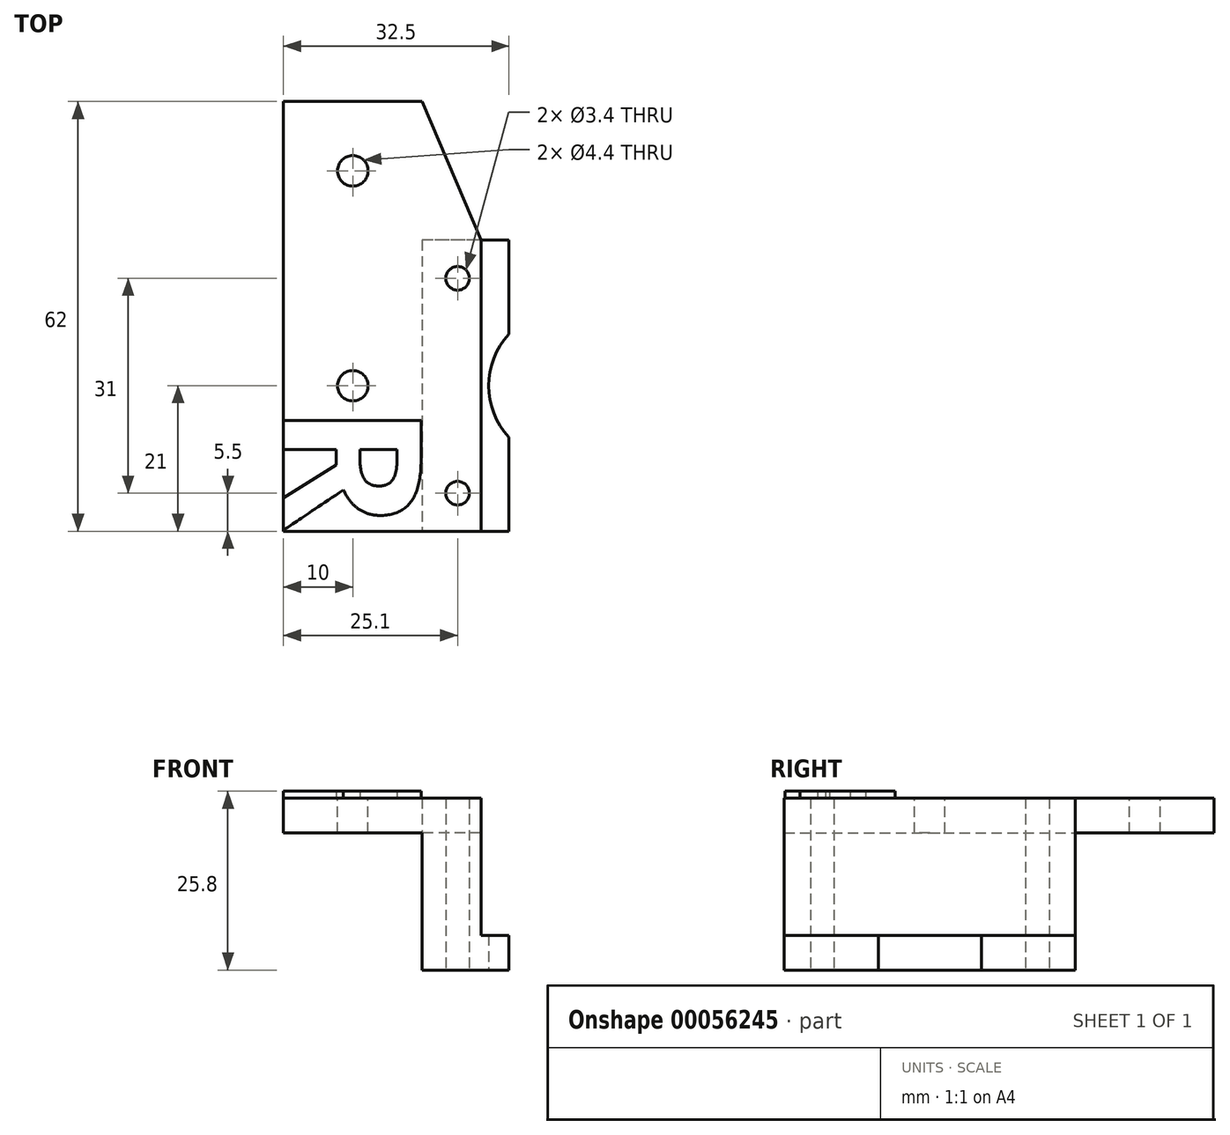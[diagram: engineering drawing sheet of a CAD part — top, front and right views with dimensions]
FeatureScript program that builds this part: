
annotation { "Feature Type Name" : "Feature", "Feature Type Description" : "" }
export const myFeature = defineFeature(function(context is Context, id is Id, definition is map)
    precondition{}
    {
        {
            var Q0;
            Q0=qCreatedBy(makeId("Front.planeOp"),FACE);
            var sketch = newSketch(context, id + "F0", { "sketchPlane" : qUnion([Q0])});
            skLineSegment(sketch, "E0", {"start": v(8.5, 24.8) * mm, "end": v(8.5, 5) * mm});
            skLineSegment(sketch, "E1", {"start": v(8.5, 5) * mm, "end": v(12.5, 5) * mm});
            skLineSegment(sketch, "E2", {"start": v(12.5, 5) * mm, "end": v(12.5, 0) * mm});
            skLineSegment(sketch, "E3", {"start": v(12.5, 0) * mm, "end": v(0, 0) * mm});
            skLineSegment(sketch, "E4", {"start": v(0, 0) * mm, "end": v(0, 24.8) * mm});
            skLineSegment(sketch, "E5", {"start": v(0, 24.8) * mm, "end": v(8.5, 24.8) * mm});
            skSolve(sketch);
        }
        {
            var Q0;
            Q0=qSketchRegion(id+"F0",true);
            extrude(context, id + "F1", {"entities" : qUnion([Q0]), "oppositeDirection" : true, "depth" : 42 * mm});
        }
        {
            var Q0;
            Q0=makeQuery(id+"F1.opExtrude","SWEPT_FACE",FACE,{"disambiguationData":[OSD([sQuery(id+"F0.wireOp",EDGE,"E3")])]});
            var sketch = newSketch(context, id + "F2", { "sketchPlane" : qUnion([Q0])});
            skCircle(sketch, "E6", {"center": v(5.1, -5.5) * mm, "radius": 1.7 * mm});
            skCircle(sketch, "E7", {"center": v(5.1, -36.5) * mm, "radius": 1.7 * mm});
            skCircle(sketch, "E8", {"center": v(20.6, -21) * mm, "radius": 11 * mm});
            skLineSegment(sketch, "E9", {"start": v(0, -21) * mm, "end": v(12.5, -21) * mm, "construction": true});
            skSolve(sketch);
        }
        {
            var Q0;
            Q0=qSketchRegion(id+"F2",true);
            extrude(context, id + "F3", {"entities" : qUnion([Q0]), "operationType" : NewBodyOperationType.REMOVE, "endBound" : BoundingType.THROUGH_ALL, "oppositeDirection" : true, "depth" : 25 * mm});
        }
        {
            var Q0;
            Q0=makeQuery(id+"F1.opExtrude","SWEPT_FACE",FACE,{"disambiguationData":[OSD([sQuery(id+"F0.wireOp",EDGE,"E4")])]});
            var sketch = newSketch(context, id + "F4", { "sketchPlane" : qUnion([Q0])});
            skLineSegment(sketch, "E10.bottom", {"start": v(0, 24.8) * mm, "end": v(-62, 24.8) * mm});
            skLineSegment(sketch, "E10.top", {"start": v(0, 19.8) * mm, "end": v(-62, 19.8) * mm});
            skLineSegment(sketch, "E10.left", {"start": v(0, 24.8) * mm, "end": v(0, 19.8) * mm});
            skLineSegment(sketch, "E10.right", {"start": v(-62, 24.8) * mm, "end": v(-62, 19.8) * mm});
            skSolve(sketch);
        }
        {
            var Q0;
            Q0=qSketchRegion(id+"F4",true);
            extrude(context, id + "F5", {"entities" : qUnion([Q0]), "operationType" : NewBodyOperationType.ADD, "depth" : 20 * mm});
        }
        {
            var Q0;
            Q0=makeQuery(id+"F5.boolean.opBoolean","MERGE",FACE,{"derivedFrom":[makeQuery(id+"F1.opExtrude","SWEPT_FACE",FACE,{"disambiguationData":[OSD([sQuery(id+"F0.wireOp",EDGE,"E5")])]}),makeQuery(id+"F5.opExtrude","SWEPT_FACE",FACE,{"disambiguationData":[OSD([sQuery(id+"F4.wireOp",EDGE,"0187bcc0-72c3-49ed-8d9d-e556f2aca4c1.bottom")])]})]});
            var sketch = newSketch(context, id + "F6", { "sketchPlane" : qUnion([Q0])});
            skCircle(sketch, "E11", {"center": v(-10, 52) * mm, "radius": 2.2 * mm});
            skCircle(sketch, "E12", {"center": v(-10, 21) * mm, "radius": 2.2 * mm});
            skPoint(sketch, "E13", {"position": v(5.1, 36.5) * mm});
            skPoint(sketch, "E14", {"position": v(5.1, 5.5) * mm});
            skPoint(sketch, "E15", {"position": v(8.5, 21) * mm});
            skSolve(sketch);
        }
        {
            var Q0;
            Q0=qSketchRegion(id+"F6",true);
            extrude(context, id + "F7", {"entities" : qUnion([Q0]), "operationType" : NewBodyOperationType.REMOVE, "oppositeDirection" : true, "depth" : 25 * mm});
        }
        {
            var Q0;
            Q0=makeQuery(id+"F5.boolean.opBoolean","MERGE",FACE,{"derivedFrom":[makeQuery(id+"F1.opExtrude","SWEPT_FACE",FACE,{"disambiguationData":[OSD([sQuery(id+"F0.wireOp",EDGE,"E5")])]}),makeQuery(id+"F5.opExtrude","SWEPT_FACE",FACE,{"disambiguationData":[OSD([sQuery(id+"F4.wireOp",EDGE,"0187bcc0-72c3-49ed-8d9d-e556f2aca4c1.bottom")])]})]});
            var sketch = newSketch(context, id + "F8", { "sketchPlane" : qUnion([Q0])});
            skText(sketch, "E16", { "text": "R", "fontName": "OpenSans-Bold.ttf"});
            const initialGuessF8  = {"E16": [-0.02, 0.01848, 0, -1, 0.02]};
            skSetInitialGuess(sketch, initialGuessF8);
            skSolve(sketch);
        }
        {
            var Q0;
            Q0=qSketchRegion(id+"F8",true);
            extrude(context, id + "F9", {"entities" : qUnion([Q0]), "operationType" : NewBodyOperationType.ADD, "depth" : 1 * mm});
        }
        {
            var Q0;
            Q0=makeQuery(id+"F5.opExtrude","CAP_FACE",FACE,{"disambiguationData":[OSD([sQuery(id+"F4.wireOp",EDGE,"E10.bottom"),sQuery(id+"F4.wireOp",EDGE,"E10.top"),sQuery(id+"F4.wireOp",EDGE,"E10.left"),sQuery(id+"F4.wireOp",EDGE,"E10.right")])],"isStart":true});
            var Q1;
            Q1=makeQuery(id+"F1.opExtrude","SWEPT_FACE",FACE,{"disambiguationData":[OSD([sQuery(id+"F0.wireOp",EDGE,"E0")])]});
            extrude(context, id + "F10", {"entities" : qUnion([Q0]), "operationType" : NewBodyOperationType.ADD, "endBound" : BoundingType.UP_TO_SURFACE, "depth" : 25 * mm, "endBoundEntityFace" : qUnion([Q1]), "offsetDistance" : 25 * mm});
        }
        {
            var Q0;
            Q0=makeQuery(id+"F10.opExtrude","CAP_EDGE",EDGE,{"disambiguationData":[OSD([sQuery(id+"F4.wireOp",EDGE,"E10.right")])],"isStart":false});
            chamfer(context, id + "F11", {"entities" : qUnion([Q0]), "chamferType" : ChamferType.TWO_OFFSETS, "width1" : 20 * mm, "oppositeDirection" : false, "width2" : 8.5 * mm, "tangentPropagation" : true});
        }
    });
